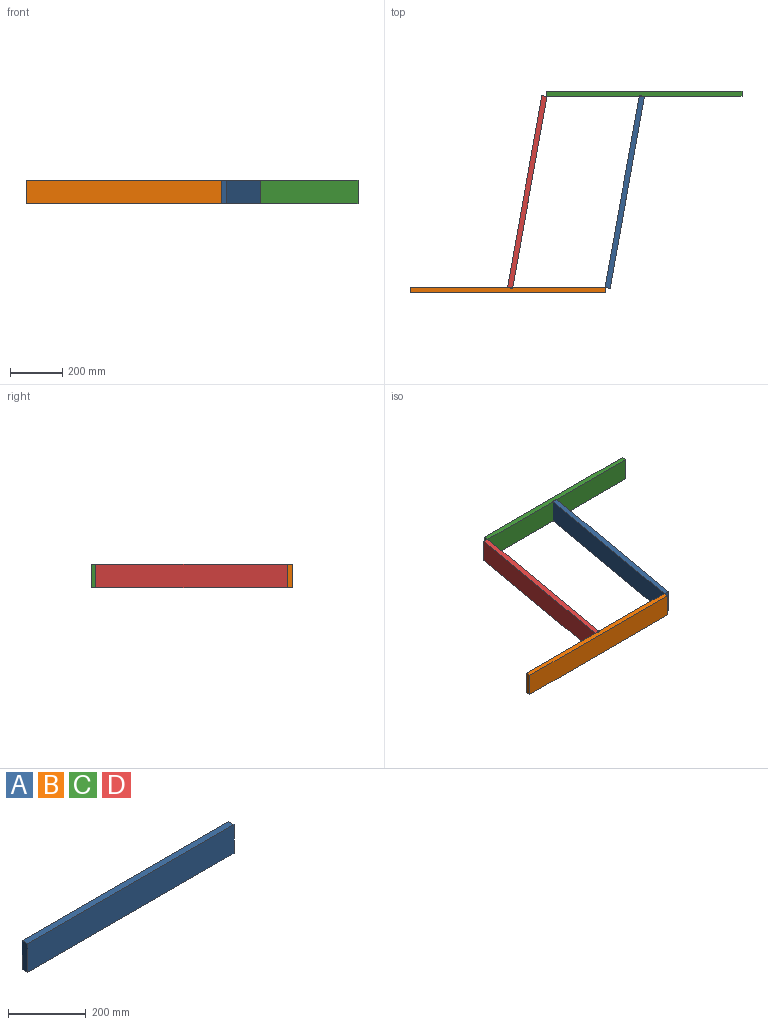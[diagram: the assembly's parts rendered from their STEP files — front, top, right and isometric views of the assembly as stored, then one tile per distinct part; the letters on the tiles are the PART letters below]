
ASSEMBLY  parts=4 mates=4
PART A: 6 faces, bbox 750x20x90 mm
  f0: plane 750x20mm, normal (0,0,-1), area 15000mm2, adj f1,f3,f4,f5
  f1: plane 90x20mm, normal (1,0,0), area 1800mm2, adj f0,f2,f4,f5
  f2: plane 750x20mm, normal (0,0,1), area 15000mm2, adj f1,f3,f4,f5
  f3: plane 90x20mm, normal (-1,0,0), area 1800mm2, adj f0,f2,f4,f5
  f4: plane 750x90mm, normal (0,-1,0), area 67500mm2, adj f0,f1,f2,f3
  f5: plane 750x90mm, normal (0,1,0), area 67500mm2, adj f0,f1,f2,f3
PART B: same geometry as A
PART C: same geometry as A
PART D: same geometry as A
PLACE A rot(axis=(0,0,-1),100.1deg) t=(-441.06,-369.14,45)mm
PLACE B t=(-901.81,-734.75,45)mm
PLACE C t=(-375,20,45)mm
PLACE D rot(axis=(0,0,-1),100.1deg) t=(-816.06,-369.14,45)mm
MATE revolute C.f0 <-> D.f0  axis (0,0,1) through (-750,0,0)mm
MATE revolute B.f0 <-> D.f0  axis (0,0,-1) through (-901.81,-734.75,0)mm
MATE revolute A.f0 <-> C.f0  axis (0,0,1) through (-375,0,0)mm
MATE revolute B.f0 <-> A.f0  axis (0,0,1) through (-526.81,-734.75,0)mm
